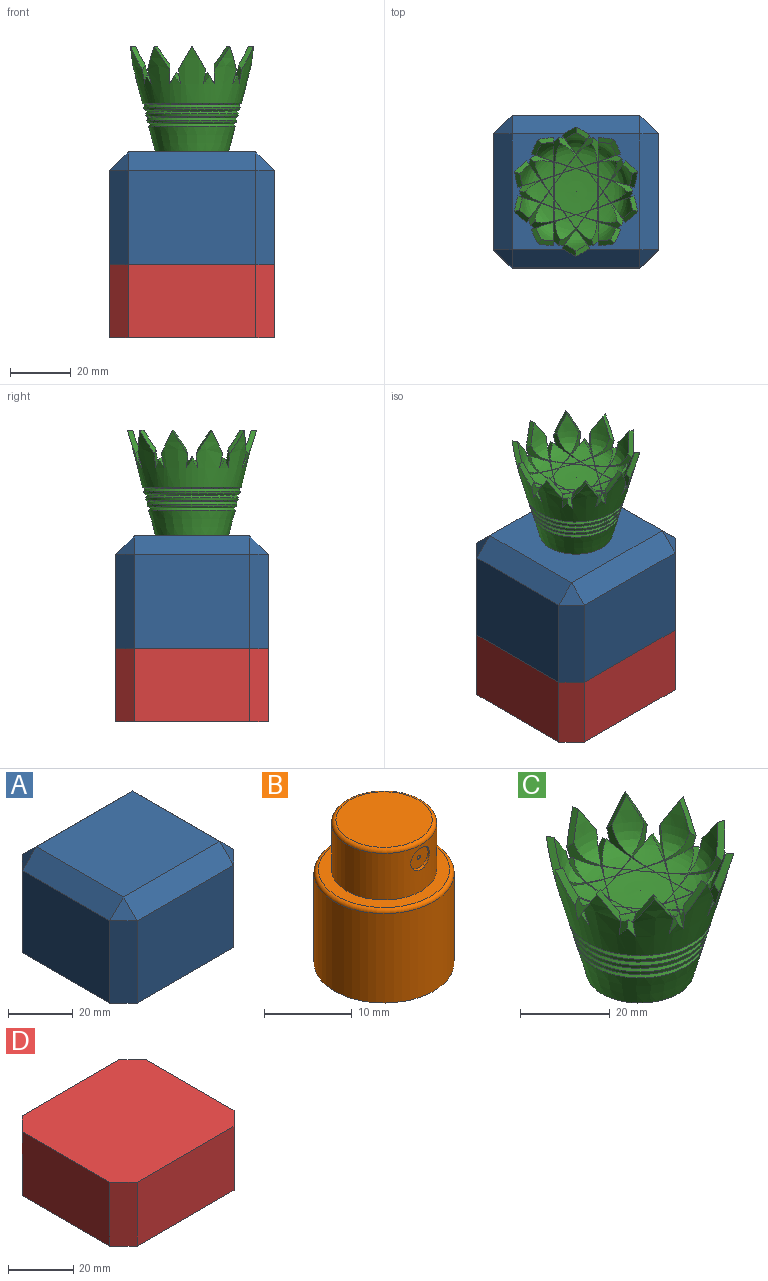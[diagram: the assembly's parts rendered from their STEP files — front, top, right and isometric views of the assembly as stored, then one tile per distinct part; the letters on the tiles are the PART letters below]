
ASSEMBLY  parts=4 mates=6
PART A: 18 faces, bbox 54x50x37 mm
  f0: plane 38x31mm, normal (1,0,0), area 1178mm2, adj f5,f6,f8,f9
  f1: plane 42x31mm, normal (0,1,0), area 1302mm2, adj f5,f8,f14,f17
  f2: plane 38x31mm, normal (-1,0,0), area 1178mm2, adj f5,f11,f15,f17
  f3: plane 42x31mm, normal (0,-1,0), area 1302mm2, adj f5,f6,f10,f11
  f4: plane 42x38mm, normal (0,0,1), area 1596mm2, adj f9,f10,f14,f15
  f5: plane 54x50mm, normal (0,0,-1), area 2628mm2, adj f0,f1,f2,f3,f6,f8,f11,f17
  f6: plane 31x6mm, normal (0.71,-0.71,0), area 263mm2, adj f0,f3,f5,f7
  f7: plane 6x6mm, normal (0.58,-0.58,0.58), area 31.2mm2, adj f6,f9,f10
  f8: plane 31x6mm, normal (0.71,0.71,0), area 263mm2, adj f0,f1,f5,f12
  f9: plane 38x6mm, normal (0.71,0,0.71), area 322.4mm2, adj f0,f4,f7,f12
  f10: plane 42x6mm, normal (0,-0.71,0.71), area 356.4mm2, adj f3,f4,f7,f13
  f11: plane 31x6mm, normal (-0.71,-0.71,0), area 263mm2, adj f2,f3,f5,f13
  f12: plane 6x6mm, normal (0.58,0.58,0.58), area 31.2mm2, adj f8,f9,f14
  f13: plane 6x6mm, normal (-0.58,-0.58,0.58), area 31.2mm2, adj f10,f11,f15
  f14: plane 42x6mm, normal (0,0.71,0.71), area 356.4mm2, adj f1,f4,f12,f16
  f15: plane 38x6mm, normal (-0.71,0,0.71), area 322.4mm2, adj f2,f4,f13,f16
  f16: plane 6x6mm, normal (-0.58,0.58,0.58), area 31.2mm2, adj f14,f15,f17
  f17: plane 31x6mm, normal (-0.71,0.71,0), area 263mm2, adj f1,f2,f5,f16
PART B: 11 faces, bbox 17.3x17.3x20 mm
  f0: cylinder r=6mm len=12mm, axis (0,0,-1), area 237.9mm2, adj f3,f5,f10
  f1: plane 11x11mm, normal (0,0,1), area 95mm2, adj f10
  f2: cylinder r=8mm len=16mm, axis (0,0,-1), area 628.3mm2, adj f4,f9
  f3: plane 15x15mm, normal (0,0,1), area 63.6mm2, adj f0,f9
  f4: plane 16x16mm, normal (0,0,-1), area 201.1mm2, adj f2
  f5: cylinder r=1.5mm len=3mm, axis (0,-1,0), area 2.9mm2, adj f0,f6
  f6: plane 3x3mm, normal (0,-1,0), area 6.9mm2, adj f5,f8
  f7: plane 0.5x0.5mm, normal (0,-1,0), area 0.2mm2, adj f8
  f8: cylinder r=0.25mm len=4.3mm, axis (0,-1,0), area 6.8mm2, adj f6,f7
  f9: torus R=7.5mm, axis (0,0,1), area 38.6mm2, adj f2,f3
  f10: torus R=5.5mm, axis (0,0,1), area 28.7mm2, adj f0,f1
PART C: 217 faces, bbox 44x44x36.3 mm
  f0: cone r=21.27mm half-angle=14.8deg, axis (0,0,1), area 1549.5mm2, adj f1,f16,f17,f18,f19,f20,f21,f22
  f1: cone r=15.29mm half-angle=67.7deg, axis (0,0,1), area 99mm2, adj f0,f2
  f2: cone r=15.91mm half-angle=38deg, axis (0,0,-1), area 98mm2, adj f1,f3
  f3: cone r=15.65mm half-angle=14.8deg, axis (0,0,1), area 99.1mm2, adj f2,f4
  f4: cone r=14.73mm half-angle=67.7deg, axis (0,0,1), area 95.4mm2, adj f3,f5
  f5: cone r=15.34mm half-angle=38deg, axis (0,0,-1), area 94.5mm2, adj f4,f6
  f6: cone r=15.09mm half-angle=14.8deg, axis (0,0,1), area 95.6mm2, adj f5,f7
  f7: cone r=14.16mm half-angle=67.7deg, axis (0,0,1), area 91.9mm2, adj f6,f8
  f8: cone r=14.78mm half-angle=38deg, axis (0,0,-1), area 90.9mm2, adj f7,f9
  f9: cone r=14.54mm half-angle=14.8deg, axis (0,0,1), area 85mm2, adj f8,f10
  f10: cone r=13.62mm half-angle=67.7deg, axis (0,0,1), area 88.5mm2, adj f9,f11
  f11: cone r=14.23mm half-angle=38deg, axis (0,0,-1), area 87.5mm2, adj f10,f12
  f12: cone r=14.23mm half-angle=14.8deg, axis (0,0,1), area 718.1mm2, adj f11,f13
  f13: plane 24x24mm, normal (0,0,-1), area 225.4mm2, adj f12,f14
  f14: cylinder r=8.5mm len=21mm, axis (0,0,-1), area 1121.5mm2, adj f13,f15
  f15: plane 17x17mm, normal (0,0,-1), area 227mm2, adj f14
  f16: plane 8.04x4.86mm, normal (-0.86,0,0.51), area 14.8mm2, adj f0,f17,f73,f188
  f17: plane 8.04x4.86mm, normal (0.86,0,0.51), area 14.8mm2, adj f0,f16,f70,f188
  f18: plane 8.04x5.58mm, normal (-0.7,0.51,0.51), area 14.8mm2, adj f0,f65,f67,f182
  f19: plane 7.89x7.71mm, normal (0.81,-0.59,0), area 18.8mm2, adj f0,f20,f59,f60,f198
  f20: plane 7.77x4.78mm, normal (-0.7,0.51,0.51), area 15.5mm2, adj f0,f19,f66,f133,f178
  f21: plane 6.38x6.32mm, normal (0.7,0.51,0.51), area 15.5mm2, adj f0,f23,f26,f92,f211
  f22: plane 8.04x4.86mm, normal (0.86,0,0.51), area 14.8mm2, adj f0,f27,f38,f206
  f23: plane 7.89x7.71mm, normal (-0.81,-0.59,0), area 18.8mm2, adj f0,f21,f27,f38,f206
  f24: plane 8.04x5.58mm, normal (-0.7,-0.51,0.51), area 14.8mm2, adj f0,f28,f30,f209
  f25: plane 9.38x7.71mm, normal (1,0,0), area 18.8mm2, adj f0,f26,f28,f30,f209
  f26: plane 8.5x4.17mm, normal (-0.86,0,0.51), area 15.5mm2, adj f0,f21,f25,f110,f211
  f27: plane 8.04x4.86mm, normal (-0.86,0,0.51), area 14.8mm2, adj f0,f22,f23,f206
  f28: plane 8.04x5.52mm, normal (0.7,0.51,0.51), area 14.8mm2, adj f0,f24,f25,f209
  f29: plane 8.47x4.17mm, normal (0.27,0.82,0.51), area 15.5mm2, adj f0,f30,f31,f113,f208
  f30: plane 9x7.71mm, normal (-0.31,-0.95,0), area 18.8mm2, adj f0,f24,f25,f29,f209
  f31: plane 7.77x4.78mm, normal (-0.7,-0.51,0.51), area 15.5mm2, adj f0,f29,f32,f114,f208
  f32: plane 7.89x7.71mm, normal (0.81,0.59,0), area 18.8mm2, adj f0,f31,f34,f35,f207
  f33: plane 7.76x4.44mm, normal (-0.27,0.82,0.51), area 15.5mm2, adj f0,f34,f61,f124,f197
  f34: plane 9x7.71mm, normal (0.31,-0.95,0), area 18.8mm2, adj f0,f32,f33,f36,f207
  f35: plane 8.04x5.12mm, normal (0.27,0.82,0.51), area 14.8mm2, adj f0,f32,f36,f207
  f36: plane 8.04x5.44mm, normal (-0.27,-0.82,0.51), area 14.8mm2, adj f0,f34,f35,f207
  f37: plane 8.04x5.44mm, normal (-0.27,0.82,0.51), area 14.8mm2, adj f0,f59,f60,f198
  f38: plane 7.89x7.71mm, normal (0.81,-0.59,0), area 18.8mm2, adj f0,f22,f23,f39,f206
  f39: plane 6.38x6.32mm, normal (-0.7,0.51,0.51), area 15.5mm2, adj f0,f38,f41,f97,f205
  f40: plane 9.38x7.71mm, normal (-1,0,0), area 18.8mm2, adj f0,f41,f56,f57,f201
  f41: plane 8.5x4.17mm, normal (0.86,0,0.51), area 15.5mm2, adj f0,f39,f40,f99,f205
  f42: plane 8.04x5.58mm, normal (0.7,-0.51,0.51), area 14.8mm2, adj f0,f56,f57,f201
  f43: plane 8.04x5.12mm, normal (-0.27,0.82,0.51), area 14.8mm2, adj f0,f45,f46,f204
  f44: plane 7.77x4.78mm, normal (0.7,-0.51,0.51), area 15.5mm2, adj f0,f46,f58,f120,f200
  f45: plane 8.04x5.44mm, normal (0.27,-0.82,0.51), area 14.8mm2, adj f0,f43,f47,f204
  f46: plane 7.89x7.71mm, normal (-0.81,0.59,0), area 18.8mm2, adj f0,f43,f44,f47,f204
  f47: plane 9x7.71mm, normal (-0.31,-0.95,0), area 18.8mm2, adj f0,f45,f46,f48,f204
  f48: plane 7.76x4.44mm, normal (0.27,0.82,0.51), area 15.5mm2, adj f0,f47,f50,f117,f203
  f49: plane 9x7.71mm, normal (-0.31,0.95,0), area 18.8mm2, adj f0,f50,f54,f55,f202
  f50: plane 7.76x4.44mm, normal (0.27,-0.82,0.51), area 15.5mm2, adj f0,f48,f49,f118,f203
  f51: plane 8.04x5.12mm, normal (-0.27,-0.82,0.51), area 14.8mm2, adj f0,f54,f55,f202
  f52: plane 8.04x5.58mm, normal (0.7,0.51,0.51), area 14.8mm2, adj f0,f62,f63,f191
  f53: plane 7.77x4.78mm, normal (0.7,0.51,0.51), area 15.5mm2, adj f0,f54,f64,f131,f192
  f54: plane 7.89x7.71mm, normal (-0.81,-0.59,0), area 18.8mm2, adj f0,f49,f51,f53,f202
  f55: plane 8.04x5.44mm, normal (0.27,0.82,0.51), area 14.8mm2, adj f0,f49,f51,f202
  f56: plane 9x7.71mm, normal (0.31,-0.95,0), area 18.8mm2, adj f0,f40,f42,f58,f201
  f57: plane 8.04x5.52mm, normal (-0.7,0.51,0.51), area 14.8mm2, adj f0,f40,f42,f201
  f58: plane 8.47x4.17mm, normal (-0.27,0.82,0.51), area 15.5mm2, adj f0,f44,f56,f106,f200
  f59: plane 9x7.71mm, normal (0.31,0.95,0), area 18.8mm2, adj f0,f19,f37,f61,f198
  f60: plane 8.04x5.12mm, normal (0.27,-0.82,0.51), area 14.8mm2, adj f0,f19,f37,f198
  f61: plane 7.76x4.44mm, normal (-0.27,-0.82,0.51), area 15.5mm2, adj f0,f33,f59,f78,f197
  f62: plane 9x7.71mm, normal (0.31,0.95,0), area 18.8mm2, adj f0,f52,f64,f68,f191
  f63: plane 8.04x5.52mm, normal (-0.7,-0.51,0.51), area 14.8mm2, adj f0,f52,f68,f191
  f64: plane 8.47x4.17mm, normal (-0.27,-0.82,0.51), area 15.5mm2, adj f0,f53,f62,f140,f192
  f65: plane 8.04x5.52mm, normal (0.7,-0.51,0.51), area 14.8mm2, adj f0,f18,f75,f182
  f66: plane 8.47x4.17mm, normal (0.27,-0.82,0.51), area 15.5mm2, adj f0,f20,f67,f173,f178
  f67: plane 9x7.71mm, normal (-0.31,0.95,0), area 18.8mm2, adj f0,f18,f66,f75,f182
  f68: plane 9.38x7.71mm, normal (-1,0,0), area 18.8mm2, adj f0,f62,f63,f69,f191
  f69: plane 8.5x4.17mm, normal (0.86,0,0.51), area 15.5mm2, adj f0,f68,f71,f143,f185
  f70: plane 7.89x7.71mm, normal (0.81,0.59,0), area 18.8mm2, adj f0,f17,f71,f73,f188
  f71: plane 6.38x6.32mm, normal (-0.7,-0.51,0.51), area 15.5mm2, adj f0,f69,f70,f168,f185
  f72: plane 6.38x6.32mm, normal (0.7,-0.51,0.51), area 15.5mm2, adj f0,f73,f74,f165,f183
  f73: plane 7.89x7.71mm, normal (-0.81,0.59,0), area 18.8mm2, adj f0,f16,f70,f72,f188
  f74: plane 8.5x4.17mm, normal (-0.86,0,0.51), area 15.5mm2, adj f0,f72,f75,f161,f183
  f75: plane 9.38x7.71mm, normal (1,0,0), area 18.8mm2, adj f0,f65,f67,f74,f182
  f76: plane 2.64x1.99mm, normal (0.81,-0.59,0), area 0.2mm2, adj f77,f125,f127,f195
  f77: plane 2.62x1.98mm, normal (-0.7,0.51,0.51), area 0.3mm2, adj f76,f134,f175,f176
  f78: plane 4.38x3.34mm, normal (0.81,-0.59,0), area 1.4mm2, adj f61,f79,f124,f197
  f79: plane 4.31x3.32mm, normal (-0.7,0.51,0.51), area 1.5mm2, adj f78,f132,f135,f180
  f80: plane 3.03x1.18mm, normal (-0.27,0.82,0.51), area 0.3mm2, adj f81,f87,f88,f216
  f81: plane 3.05x1.18mm, normal (0.31,-0.95,0), area 0.2mm2, adj f80,f82,f96,f214
  f82: plane 3.05x1.18mm, normal (-0.31,-0.95,0), area 0.2mm2, adj f81,f83,f93,f214
  f83: plane 3.03x1.18mm, normal (0.27,0.82,0.51), area 0.3mm2, adj f82,f85,f95,f215
  f84: plane 5.19x2.19mm, normal (-0.27,0.82,0.51), area 0.1mm2, adj f85,f86,f91,f177
  f85: plane 5.19x2.17mm, normal (0.31,-0.95,0), area 0.1mm2, adj f83,f84,f95,f215
  f86: plane 5.19x2.19mm, normal (0.27,0.82,0.51), area 0.1mm2, adj f84,f87,f100,f177
  f87: plane 5.19x2.17mm, normal (-0.31,-0.95,0), area 0.1mm2, adj f80,f86,f88,f216
  f88: plane 2.62x2.01mm, normal (0.7,0.51,0.51), area 0.3mm2, adj f80,f87,f89,f216
  f89: plane 2.64x1.99mm, normal (-0.81,-0.59,0), area 0.2mm2, adj f88,f98,f105,f212
  f90: plane 4.52x3.48mm, normal (0.81,-0.59,0), area 0.1mm2, adj f91,f109,f126,f196
  f91: plane 4.53x3.5mm, normal (-0.7,0.51,0.51), area 0.1mm2, adj f84,f90,f174,f177
  f92: plane 4.38x3.34mm, normal (0.81,-0.59,0), area 1.4mm2, adj f21,f93,f110,f211
  f93: plane 4.33x3.27mm, normal (-0.7,0.51,0.51), area 1.5mm2, adj f82,f92,f96,f214
  f94: plane 2.64x1.99mm, normal (0.81,-0.59,0), area 0.2mm2, adj f95,f108,f111,f210
  f95: plane 2.62x2.01mm, normal (-0.7,0.51,0.51), area 0.3mm2, adj f83,f85,f94,f215
  f96: plane 4.33x3.27mm, normal (0.7,0.51,0.51), area 1.5mm2, adj f81,f93,f97,f214
  f97: plane 4.38x3.34mm, normal (-0.81,-0.59,0), area 1.4mm2, adj f39,f96,f99,f205
  f98: plane 4.97x2.02mm, normal (-0.27,0.82,0.51), area 1.5mm2, adj f89,f99,f107,f212
  f99: plane 5.05x2.03mm, normal (0.31,-0.95,0), area 1.4mm2, adj f41,f97,f98,f205
  f100: plane 4.53x3.5mm, normal (0.7,0.51,0.51), area 0.1mm2, adj f86,f101,f137,f177
  f101: plane 4.52x3.48mm, normal (-0.81,-0.59,0), area 0.1mm2, adj f100,f103,f104,f213
  f102: plane 3.19x0.42mm, normal (-1,0,0), area 0.2mm2, adj f103,f121,f122,f199
  f103: plane 3.18x0.4mm, normal (0.86,0,0.51), area 0.3mm2, adj f101,f102,f104,f213
  f104: plane 3.03x1.23mm, normal (0.27,0.82,0.51), area 0.3mm2, adj f101,f103,f105,f213
  f105: plane 3.05x1.18mm, normal (-0.31,-0.95,0), area 0.2mm2, adj f89,f104,f107,f212
  f106: plane 5.28x1.14mm, normal (-1,0,0), area 1.4mm2, adj f58,f107,f120,f200
  f107: plane 5.2x1.02mm, normal (0.86,0,0.51), area 1.5mm2, adj f98,f105,f106,f212
  f108: plane 3.05x1.18mm, normal (0.31,-0.95,0), area 0.2mm2, adj f94,f109,f112,f210
  f109: plane 3.03x1.23mm, normal (-0.27,0.82,0.51), area 0.3mm2, adj f90,f108,f126,f196
  f110: plane 5.05x2.03mm, normal (-0.31,-0.95,0), area 1.4mm2, adj f26,f92,f111,f211
  f111: plane 4.97x2.02mm, normal (0.27,0.82,0.51), area 1.5mm2, adj f94,f110,f112,f210
  f112: plane 5.2x1.02mm, normal (-0.86,0,0.51), area 1.5mm2, adj f108,f111,f113,f210
  f113: plane 5.28x1.14mm, normal (1,0,0), area 1.4mm2, adj f29,f112,f114,f208
  f114: plane 5.05x2.03mm, normal (0.31,-0.95,0), area 1.4mm2, adj f31,f113,f115,f208
  f115: plane 4.98x2.12mm, normal (-0.27,0.82,0.51), area 1.5mm2, adj f114,f125,f127,f195
  f116: plane 4.31x3.32mm, normal (0.7,-0.51,0.51), area 1.5mm2, adj f117,f121,f122,f199
  f117: plane 4.38x3.34mm, normal (-0.81,0.59,0), area 1.4mm2, adj f48,f116,f118,f203
  f118: plane 4.38x3.34mm, normal (-0.81,-0.59,0), area 1.4mm2, adj f50,f117,f119,f203
  f119: plane 4.31x3.32mm, normal (0.7,0.51,0.51), area 1.5mm2, adj f118,f129,f130,f193
  f120: plane 5.05x2.03mm, normal (-0.31,-0.95,0), area 1.4mm2, adj f44,f106,f121,f200
  f121: plane 4.98x2.12mm, normal (0.27,0.82,0.51), area 1.5mm2, adj f102,f116,f120,f199
  f122: plane 2.64x1.99mm, normal (-0.81,-0.59,0), area 0.2mm2, adj f102,f116,f123,f199
  f123: plane 2.62x1.98mm, normal (0.7,0.51,0.51), area 0.3mm2, adj f122,f128,f136,f194
  f124: plane 4.38x3.34mm, normal (0.81,0.59,0), area 1.4mm2, adj f33,f78,f125,f197
  f125: plane 4.31x3.32mm, normal (-0.7,-0.51,0.51), area 1.5mm2, adj f76,f115,f124,f195
  f126: plane 3.18x0.4mm, normal (-0.86,0,0.51), area 0.3mm2, adj f90,f109,f127,f196
  f127: plane 3.19x0.42mm, normal (1,0,0), area 0.2mm2, adj f76,f115,f126,f195
  f128: plane 2.62x1.98mm, normal (0.7,-0.51,0.51), area 0.3mm2, adj f123,f129,f136,f194
  f129: plane 2.64x1.99mm, normal (-0.81,0.59,0), area 0.2mm2, adj f119,f128,f138,f193
  f130: plane 4.98x2.12mm, normal (0.27,-0.82,0.51), area 1.5mm2, adj f119,f131,f138,f193
  f131: plane 5.05x2.03mm, normal (-0.31,0.95,0), area 1.4mm2, adj f53,f130,f140,f192
  f132: plane 4.98x2.12mm, normal (-0.27,-0.82,0.51), area 1.5mm2, adj f79,f133,f171,f180
  f133: plane 5.05x2.03mm, normal (0.31,0.95,0), area 1.4mm2, adj f20,f132,f173,f178
  f134: plane 2.62x1.98mm, normal (-0.7,-0.51,0.51), area 0.3mm2, adj f77,f135,f175,f176
  f135: plane 2.64x1.99mm, normal (0.81,0.59,0), area 0.2mm2, adj f79,f134,f171,f180
  f136: plane 5.42x0.76mm, normal (-1,0,0), area 0.1mm2, adj f123,f128,f137,f194
  f137: plane 5.42x0.76mm, normal (0.86,0,0.51), area 0.1mm2, adj f100,f136,f147,f177
  f138: plane 3.19x0.42mm, normal (-1,0,0), area 0.2mm2, adj f129,f130,f139,f193
  f139: plane 3.18x0.4mm, normal (0.86,0,0.51), area 0.3mm2, adj f138,f145,f146,f190
  f140: plane 5.28x1.14mm, normal (-1,0,0), area 1.4mm2, adj f64,f131,f141,f192
  f141: plane 5.2x1.02mm, normal (0.86,0,0.51), area 1.5mm2, adj f140,f142,f144,f187
  f142: plane 4.97x2.02mm, normal (-0.27,-0.82,0.51), area 1.5mm2, adj f141,f143,f166,f187
  f143: plane 5.05x2.03mm, normal (0.31,0.95,0), area 1.4mm2, adj f69,f142,f168,f185
  f144: plane 3.05x1.18mm, normal (-0.31,0.95,0), area 0.2mm2, adj f141,f145,f166,f187
  f145: plane 3.03x1.23mm, normal (0.27,-0.82,0.51), area 0.3mm2, adj f139,f144,f146,f190
  f146: plane 4.52x3.48mm, normal (-0.81,0.59,0), area 0.1mm2, adj f139,f145,f147,f190
  f147: plane 4.53x3.5mm, normal (0.7,-0.51,0.51), area 0.1mm2, adj f137,f146,f154,f177
  f148: plane 3.03x1.18mm, normal (0.27,-0.82,0.51), area 0.3mm2, adj f149,f150,f151,f189
  f149: plane 2.62x2.01mm, normal (-0.7,-0.51,0.51), area 0.3mm2, adj f148,f150,f152,f189
  f150: plane 5.19x2.17mm, normal (0.31,0.95,0), area 0.1mm2, adj f148,f149,f157,f189
  f151: plane 3.05x1.18mm, normal (-0.31,0.95,0), area 0.2mm2, adj f148,f153,f164,f184
  f152: plane 2.64x1.99mm, normal (0.81,0.59,0), area 0.2mm2, adj f149,f160,f162,f179
  f153: plane 3.05x1.18mm, normal (0.31,0.95,0), area 0.2mm2, adj f151,f156,f169,f184
  f154: plane 5.19x2.19mm, normal (0.27,-0.82,0.51), area 0.1mm2, adj f147,f155,f157,f177
  f155: plane 5.19x2.17mm, normal (-0.31,0.95,0), area 0.1mm2, adj f154,f156,f167,f186
  f156: plane 3.03x1.18mm, normal (-0.27,-0.82,0.51), area 0.3mm2, adj f153,f155,f167,f186
  f157: plane 5.19x2.19mm, normal (-0.27,-0.82,0.51), area 0.1mm2, adj f150,f154,f159,f177
  f158: plane 4.52x3.48mm, normal (0.81,0.59,0), area 0.1mm2, adj f159,f163,f170,f181
  f159: plane 4.53x3.5mm, normal (-0.7,-0.51,0.51), area 0.1mm2, adj f157,f158,f174,f177
  f160: plane 3.05x1.18mm, normal (0.31,0.95,0), area 0.2mm2, adj f152,f163,f172,f179
  f161: plane 5.05x2.03mm, normal (-0.31,0.95,0), area 1.4mm2, adj f74,f162,f165,f183
  f162: plane 4.97x2.02mm, normal (0.27,-0.82,0.51), area 1.5mm2, adj f152,f161,f172,f179
  f163: plane 3.03x1.23mm, normal (-0.27,-0.82,0.51), area 0.3mm2, adj f158,f160,f170,f181
  f164: plane 4.33x3.27mm, normal (-0.7,-0.51,0.51), area 1.5mm2, adj f151,f165,f169,f184
  f165: plane 4.38x3.34mm, normal (0.81,0.59,0), area 1.4mm2, adj f72,f161,f164,f183
  f166: plane 2.64x1.99mm, normal (-0.81,0.59,0), area 0.2mm2, adj f142,f144,f167,f187
  f167: plane 2.62x2.01mm, normal (0.7,-0.51,0.51), area 0.3mm2, adj f155,f156,f166,f186
  f168: plane 4.38x3.34mm, normal (-0.81,0.59,0), area 1.4mm2, adj f71,f143,f169,f185
  f169: plane 4.33x3.27mm, normal (0.7,-0.51,0.51), area 1.5mm2, adj f153,f164,f168,f184
  f170: plane 3.18x0.4mm, normal (-0.86,0,0.51), area 0.3mm2, adj f158,f163,f171,f181
  f171: plane 3.19x0.42mm, normal (1,0,0), area 0.2mm2, adj f132,f135,f170,f180
  f172: plane 5.2x1.02mm, normal (-0.86,0,0.51), area 1.5mm2, adj f160,f162,f173,f179
  f173: plane 5.28x1.14mm, normal (1,0,0), area 1.4mm2, adj f66,f133,f172,f178
  f174: plane 4.88x0.23mm, normal (-0.86,0,0.51), area 0.1mm2, adj f91,f159,f175,f177
  f175: plane 5.42x0.76mm, normal (1,0,0), area 0.1mm2, adj f77,f134,f174,f176
  f176: revolved ~5.38x1.61mm, area 3.1mm2, adj f77,f134,f175
  f177: revolved ~15.15x15.15mm, area 179.6mm2, adj f84,f86,f91,f100,f137,f147,f154,f157
  f178: revolved ~10.4x10.37mm, area 34.3mm2, adj f20,f66,f133,f173
  f179: revolved ~7.08x6.67mm, area 12.4mm2, adj f152,f160,f162,f172
  f180: revolved ~6.8x5.6mm, area 12.4mm2, adj f79,f132,f135,f171
  f181: revolved ~4.75x3.91mm, area 3.1mm2, adj f158,f163,f170
  f182: revolved ~11.64x9.48mm, area 51.5mm2, adj f18,f65,f67,f75
  f183: revolved ~9.4x9.33mm, area 34.3mm2, adj f72,f74,f161,f165
  f184: revolved ~7.12x4.54mm, area 12.4mm2, adj f151,f153,f164,f169
  f185: revolved ~9.4x9.33mm, area 34.3mm2, adj f69,f71,f143,f168
  f186: revolved ~5.12x2.68mm, area 3.1mm2, adj f155,f156,f167
  f187: revolved ~7.08x6.67mm, area 12.4mm2, adj f141,f142,f144,f166
  f188: revolved ~11.64x7.98mm, area 51.5mm2, adj f16,f17,f70,f73
  f189: revolved ~5.12x2.68mm, area 3.1mm2, adj f148,f149,f150
  f190: revolved ~4.75x3.91mm, area 3.1mm2, adj f139,f145,f146
  f191: revolved ~11.64x9.48mm, area 51.5mm2, adj f52,f62,f63,f68
  f192: revolved ~10.4x10.37mm, area 34.3mm2, adj f53,f64,f131,f140
  f193: revolved ~6.8x5.6mm, area 12.4mm2, adj f119,f129,f130,f138
  f194: revolved ~5.38x1.61mm, area 3.1mm2, adj f123,f128,f136
  f195: revolved ~6.8x5.6mm, area 12.4mm2, adj f76,f115,f125,f127
  f196: revolved ~4.75x3.91mm, area 3.1mm2, adj f90,f109,f126
  f197: revolved ~9.75x8.11mm, area 34.3mm2, adj f33,f61,f78,f124
  f198: revolved ~11.64x8.66mm, area 51.5mm2, adj f19,f37,f59,f60
  f199: revolved ~6.8x5.6mm, area 12.4mm2, adj f102,f116,f121,f122
  f200: revolved ~10.4x10.37mm, area 34.3mm2, adj f44,f58,f106,f120
  f201: revolved ~11.64x9.48mm, area 51.5mm2, adj f40,f42,f56,f57
  f202: revolved ~11.64x8.66mm, area 51.5mm2, adj f49,f51,f54,f55
  f203: revolved ~9.75x8.11mm, area 34.3mm2, adj f48,f50,f117,f118
  f204: revolved ~11.64x8.66mm, area 51.5mm2, adj f43,f45,f46,f47
  f205: revolved ~9.4x9.33mm, area 34.3mm2, adj f39,f41,f97,f99
  f206: revolved ~11.64x7.98mm, area 51.5mm2, adj f22,f23,f27,f38
  f207: revolved ~11.64x8.66mm, area 51.5mm2, adj f32,f34,f35,f36
  f208: revolved ~10.4x10.37mm, area 34.3mm2, adj f29,f31,f113,f114
  f209: revolved ~11.64x9.48mm, area 51.5mm2, adj f24,f25,f28,f30
  f210: revolved ~7.08x6.67mm, area 12.4mm2, adj f94,f108,f111,f112
  f211: revolved ~9.4x9.33mm, area 34.3mm2, adj f21,f26,f92,f110
  f212: revolved ~7.08x6.67mm, area 12.4mm2, adj f89,f98,f105,f107
  f213: revolved ~4.75x3.91mm, area 3.1mm2, adj f101,f103,f104
  f214: revolved ~7.12x4.54mm, area 12.4mm2, adj f81,f82,f93,f96
  f215: revolved ~5.12x2.68mm, area 3.1mm2, adj f83,f85,f95
  f216: revolved ~5.12x2.68mm, area 3.1mm2, adj f80,f87,f88
PART D: 10 faces, bbox 54x50x24 mm
  f0: plane 38x24mm, normal (1,0,0), area 912mm2, adj f4,f5,f7,f8
  f1: plane 42x24mm, normal (0,1,0), area 1008mm2, adj f4,f5,f8,f9
  f2: plane 38x24mm, normal (-1,0,0), area 912mm2, adj f4,f5,f6,f9
  f3: plane 42x24mm, normal (0,-1,0), area 1008mm2, adj f4,f5,f6,f7
  f4: plane 54x50mm, normal (0,0,1), area 2628mm2, adj f0,f1,f2,f3,f6,f7,f8,f9
  f5: plane 54x50mm, normal (0,0,-1), area 2628mm2, adj f0,f1,f2,f3,f6,f7,f8,f9
  f6: plane 24x6mm, normal (-0.71,-0.71,0), area 203.6mm2, adj f2,f3,f4,f5
  f7: plane 24x6mm, normal (0.71,-0.71,0), area 203.6mm2, adj f0,f3,f4,f5
  f8: plane 24x6mm, normal (0.71,0.71,0), area 203.6mm2, adj f0,f1,f4,f5
  f9: plane 24x6mm, normal (-0.71,0.71,0), area 203.6mm2, adj f1,f2,f4,f5
PLACE A t=(-9.74,4.97,-2.6)mm fixed
PLACE B t=(-9.74,4.97,34.4)mm
PLACE C t=(-9.74,4.97,34.4)mm
PLACE D t=(-9.74,4.97,-26.6)mm
MATE parallel C.f0 <-> B.f0  axis (0,0,-1) through (-9.74,4.97,55.4)mm
MATE parallel A.f5 <-> D.f4  axis (0,0,-1) through (-9.74,4.97,-2.6)mm
MATE parallel B.f0 <-> A.f4  axis (0,0,-1) through (-9.74,4.97,34.4)mm
MATE parallel B.f0 <-> A.f4  axis (0,0,-1) through (-9.74,4.97,34.4)mm
MATE parallel C.f0 <-> B.f0  axis (0,0,-1) through (-9.74,4.97,34.4)mm
MATE parallel A.f5 <-> D.f4  axis (0,0,-1) through (-9.74,4.97,-2.6)mm
